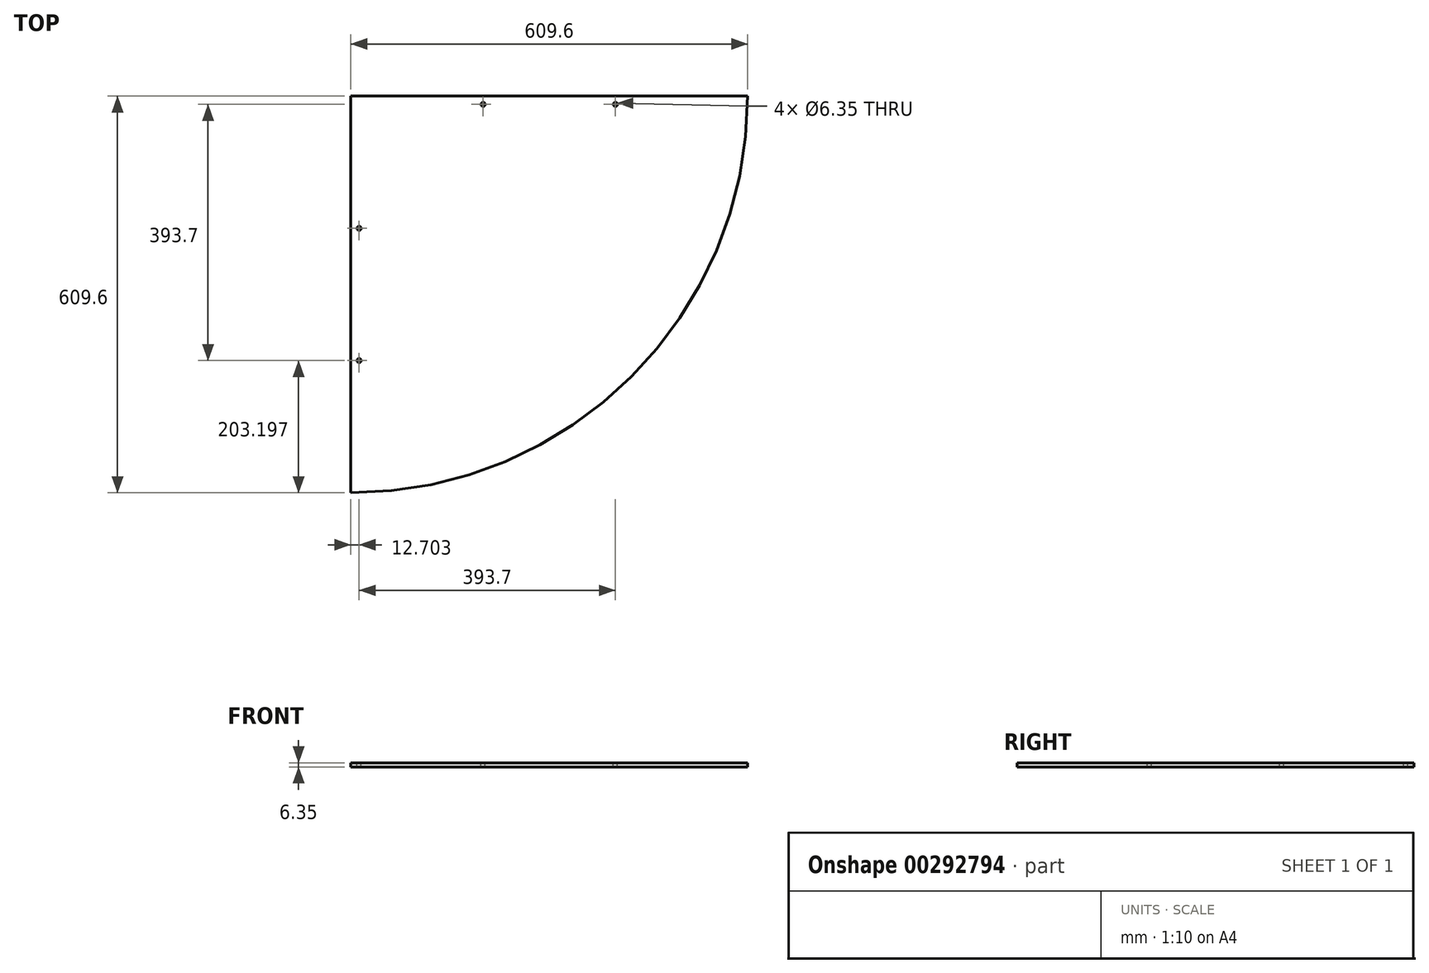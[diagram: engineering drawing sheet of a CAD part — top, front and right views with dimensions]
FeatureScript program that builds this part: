
annotation { "Feature Type Name" : "Feature", "Feature Type Description" : "" }
export const myFeature = defineFeature(function(context is Context, id is Id, definition is map)
    precondition{}
    {
        {
            var Q0;
            Q0=qCreatedBy(makeId("Top.planeOp"),FACE);
            var sketch = newSketch(context, id + "F0", { "sketchPlane" : qUnion([Q0])});
            skLineSegment(sketch, "E0", {"start": v(-322.04, 328) * mm, "end": v(-322.04, -281.6) * mm});
            skLineSegment(sketch, "E1", {"start": v(-322.04, -281.6) * mm, "end": v(-322.04, 328) * mm});
            skLineSegment(sketch, "E2", {"start": v(287.56, 328) * mm, "end": v(-322.04, 328) * mm});
            skArc(sketch, "E3", {"start": v(287.56, 328) * mm, "mid": v(109.01, -103.05) * mm, "end": v(-322.04, -281.6) * mm});
            skSolve(sketch);
        }
        {
            var Q0;
            Q0 = qSketchRegion(id + "F0", true);
            extrude(context, id + "F1", {"entities" : qUnion([Q0]), "depth" : 6.35 * mm});
        }
        {
            var Q0;
            Q0=makeQuery(id+"F1.opExtrude","CAP_FACE",FACE,{"disambiguationData":[OSD([sQuery(id+"F0.wireOp",EDGE,"E1"),sQuery(id+"F0.wireOp",EDGE,"E2"),sQuery(id+"F0.wireOp",EDGE,"E3")])],"isStart":false});
            var sketch = newSketch(context, id + "F2", { "sketchPlane" : qUnion([Q0])});
            skCircle(sketch, "E4", {"center": v(-309.34, 124.8) * mm, "radius": 3.18 * mm});
            skCircle(sketch, "E5", {"center": v(-309.34, -78.4) * mm, "radius": 3.18 * mm});
            skCircle(sketch, "E6", {"center": v(-118.84, 315.3) * mm, "radius": 3.18 * mm});
            skCircle(sketch, "E7", {"center": v(84.36, 315.3) * mm, "radius": 3.18 * mm});
            skSolve(sketch);
        }
        {
            var Q0;
            Q0=sQuery(id+"F2.wireOp",VERTEX,"E6.center");
            var Q1;
            Q1=sQuery(id+"F2.wireOp",VERTEX,"E7.center");
            var Q2;
            Q2=sQuery(id+"F2.wireOp",VERTEX,"E5.center");
            var Q3;
            Q3=sQuery(id+"F2.wireOp",VERTEX,"E4.center");
            var Q4;
            Q4=makeQuery(id+"F1.opExtrude","SWEPT_BODY",BODY,{"disambiguationData":[OSD([sQuery(id+"F0.wireOp",EDGE,"E1"),sQuery(id+"F0.wireOp",EDGE,"E2"),sQuery(id+"F0.wireOp",EDGE,"E3")])]});
            hole(context, id + "F3", {"style" : HoleStyle.SIMPLE, "endStyle" : HoleEndStyle.THROUGH, "holeDiameter" : 6.35 * mm, "tappedDepth" : 12.7 * mm, "tapClearance" : 3, "locations" : qUnion([Q0, Q1, Q2, Q3]), "scope" : qUnion([Q4])});
        }
    });
